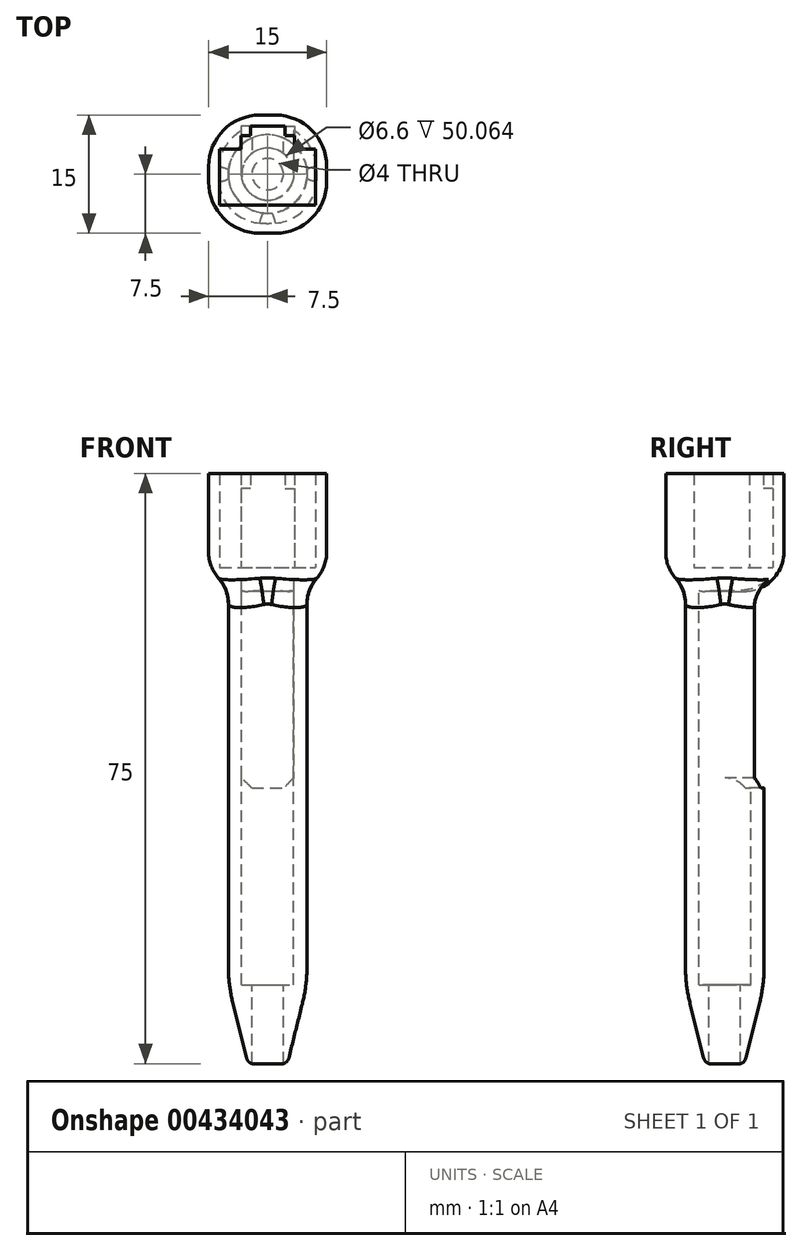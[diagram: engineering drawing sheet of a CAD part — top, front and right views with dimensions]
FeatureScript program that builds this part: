
annotation { "Feature Type Name" : "Feature", "Feature Type Description" : "" }
export const myFeature = defineFeature(function(context is Context, id is Id, definition is map)
    precondition{}
    {
        {
            var Q0;
            Q0=qCreatedBy(makeId("Top.planeOp"),FACE);
            var sketch = newSketch(context, id + "F0", { "sketchPlane" : qUnion([Q0])});
            skLineSegment(sketch, "E0.bottom", {"start": v(7.5, 7.5) * mm, "end": v(-7.5, 7.5) * mm});
            skLineSegment(sketch, "E0.top", {"start": v(7.5, -7.5) * mm, "end": v(-7.5, -7.5) * mm});
            skLineSegment(sketch, "E0.left", {"start": v(7.5, 7.5) * mm, "end": v(7.5, -7.5) * mm});
            skLineSegment(sketch, "E0.right", {"start": v(-7.5, 7.5) * mm, "end": v(-7.5, -7.5) * mm});
            skPoint(sketch, "E0.middle", {"position": v(0, 0) * mm});
            skLineSegment(sketch, "E1.bottom", {"start": v(-6.1, -3.94) * mm, "end": v(6.1, -3.94) * mm});
            skLineSegment(sketch, "E1.top", {"start": v(-6.1, 3.16) * mm, "end": v(6.1, 3.16) * mm});
            skLineSegment(sketch, "E1.left", {"start": v(-6.1, -3.94) * mm, "end": v(-6.1, 3.16) * mm});
            skLineSegment(sketch, "E1.right", {"start": v(6.1, -3.94) * mm, "end": v(6.1, 3.16) * mm});
            skLineSegment(sketch, "E2.bottom", {"start": v(-6.1, 3.16) * mm, "end": v(-3.4, 3.16) * mm, "construction": true});
            skLineSegment(sketch, "E2.top", {"start": v(-6.1, 3.16) * mm, "end": v(-3.4, 3.16) * mm, "construction": true});
            skLineSegment(sketch, "E2.left", {"start": v(-6.1, 3.16) * mm, "end": v(-6.1, 3.16) * mm});
            skLineSegment(sketch, "E2.right", {"start": v(-3.4, 3.16) * mm, "end": v(-3.4, 3.16) * mm});
            skLineSegment(sketch, "E3.bottom", {"start": v(6.1, 3.16) * mm, "end": v(3.4, 3.16) * mm, "construction": true});
            skLineSegment(sketch, "E3.top", {"start": v(6.1, 3.16) * mm, "end": v(3.4, 3.16) * mm, "construction": true});
            skLineSegment(sketch, "E3.left", {"start": v(6.1, 3.16) * mm, "end": v(6.1, 3.16) * mm});
            skLineSegment(sketch, "E3.right", {"start": v(3.4, 3.16) * mm, "end": v(3.4, 3.16) * mm});
            skLineSegment(sketch, "E4", {"start": v(-3.4, 3.16) * mm, "end": v(-3.4, 6.1) * mm});
            skLineSegment(sketch, "E5", {"start": v(-3.4, 6.1) * mm, "end": v(3.4, 6.1) * mm});
            skLineSegment(sketch, "E6", {"start": v(3.4, 3.16) * mm, "end": v(3.4, 6.1) * mm});
            skLineSegment(sketch, "E7", {"start": v(-6.1, -3.94) * mm, "end": v(-6.1, 1.06) * mm, "construction": true});
            skLineSegment(sketch, "E8", {"start": v(-7.5, 7.5) * mm, "end": v(0, 7.5) * mm, "construction": true});
            skLineSegment(sketch, "E9", {"start": v(0, 7.5) * mm, "end": v(0, -7.5) * mm, "construction": true});
            skLineSegment(sketch, "E10", {"start": v(0, 3.16) * mm, "end": v(0, -3.94) * mm, "construction": true});
            skSolve(sketch);
        }
        {
            var Q0;
            Q0=makeQuery(id+"F0.imprint","IMPRINT",FACE,{"disambiguationData":[TD([[makeQuery(id+"F0.imprint","IMPRINT",EDGE,{"derivedFrom":sQuery(id+"F0.wireOp",EDGE,"E0.bottom")}),1.0]])]});
            extrude(context, id + "F1", {"entities" : qUnion([Q0]), "depth" : 12 * mm});
        }
        {
            var Q0;
            Q0=makeQuery(id+"F1.opExtrude","SWEPT_FACE",FACE,{"disambiguationData":[OSD([sQuery(id+"F0.wireOp",EDGE,"E6")])]});
            var sketch = newSketch(context, id + "F2", { "sketchPlane" : qUnion([Q0])});
            skLineSegment(sketch, "E11.bottom", {"start": v(-6.1, 12) * mm, "end": v(-4.9, 12) * mm});
            skLineSegment(sketch, "E11.top", {"start": v(-6.1, 10.05) * mm, "end": v(-4.9, 10.05) * mm});
            skLineSegment(sketch, "E11.left", {"start": v(-6.1, 12) * mm, "end": v(-6.1, 10.05) * mm});
            skLineSegment(sketch, "E11.right", {"start": v(-4.9, 12) * mm, "end": v(-4.9, 10.05) * mm});
            skSolve(sketch);
        }
        {
            var Q0;
            Q0 = qSketchRegion(id + "F2", true);
            extrude(context, id + "F3", {"entities" : qUnion([Q0]), "operationType" : NewBodyOperationType.ADD, "depth" : 1.21 * mm});
        }
        {
            var Q0;
            Q0=makeQuery(id+"F1.opExtrude","SWEPT_FACE",FACE,{"disambiguationData":[OSD([sQuery(id+"F0.wireOp",EDGE,"E4")])]});
            var sketch = newSketch(context, id + "F4", { "sketchPlane" : qUnion([Q0])});
            skLineSegment(sketch, "E12.bottom", {"start": v(6.1, 12) * mm, "end": v(4.9, 12) * mm});
            skLineSegment(sketch, "E12.top", {"start": v(6.1, 10.05) * mm, "end": v(4.9, 10.05) * mm});
            skLineSegment(sketch, "E12.left", {"start": v(6.1, 12) * mm, "end": v(6.1, 10.05) * mm});
            skLineSegment(sketch, "E12.right", {"start": v(4.9, 12) * mm, "end": v(4.9, 10.05) * mm});
            skSolve(sketch);
        }
        {
            var Q0;
            Q0=makeQuery(id+"F4.imprint","IMPRINT",FACE,{"disambiguationData":[TD([[makeQuery(id+"F4.imprint","IMPRINT",EDGE,{"derivedFrom":sQuery(id+"F4.wireOp",EDGE,"E12.bottom")}),-1.0]])]});
            extrude(context, id + "F5", {"entities" : qUnion([Q0]), "operationType" : NewBodyOperationType.ADD, "depth" : 1.21 * mm});
        }
        {
            var Q0;
            Q0=makeQuery(id+"F1.opExtrude","CAP_FACE",FACE,{"disambiguationData":[OSD([sQuery(id+"F0.wireOp",EDGE,"E0.bottom"),sQuery(id+"F0.wireOp",EDGE,"E0.top"),sQuery(id+"F0.wireOp",EDGE,"E0.left"),sQuery(id+"F0.wireOp",EDGE,"E0.right"),sQuery(id+"F0.wireOp",EDGE,"E1.bottom"),sQuery(id+"F0.wireOp",EDGE,"E1.top"),sQuery(id+"F0.wireOp",EDGE,"E1.left"),sQuery(id+"F0.wireOp",EDGE,"E1.right"),sQuery(id+"F0.wireOp",EDGE,"E4"),sQuery(id+"F0.wireOp",EDGE,"E5"),sQuery(id+"F0.wireOp",EDGE,"E6")])],"isStart":true});
            var sketch = newSketch(context, id + "F6", { "sketchPlane" : qUnion([Q0])});
            skLineSegment(sketch, "E13.bottom", {"start": v(-7.5, 7.5) * mm, "end": v(7.5, 7.5) * mm});
            skLineSegment(sketch, "E13.top", {"start": v(-7.5, -7.5) * mm, "end": v(7.5, -7.5) * mm});
            skLineSegment(sketch, "E13.left", {"start": v(-7.5, 7.5) * mm, "end": v(-7.5, -7.5) * mm});
            skLineSegment(sketch, "E13.right", {"start": v(7.5, 7.5) * mm, "end": v(7.5, -7.5) * mm});
            skSolve(sketch);
        }
        {
            var Q0;
            Q0 = qSketchRegion(id + "F6", true);
            extrude(context, id + "F7", {"entities" : qUnion([Q0]), "operationType" : NewBodyOperationType.ADD, "depth" : 3 * mm});
        }
        {
            var Q0;
            Q0=makeQuery(id+"F7.opExtrude","CAP_FACE",FACE,{"disambiguationData":[OSD([sQuery(id+"F6.wireOp",EDGE,"E13.bottom"),sQuery(id+"F6.wireOp",EDGE,"E13.top"),sQuery(id+"F6.wireOp",EDGE,"E13.left"),sQuery(id+"F6.wireOp",EDGE,"E13.right")])],"isStart":false});
            var sketch = newSketch(context, id + "F8", { "sketchPlane" : qUnion([Q0])});
            skCircle(sketch, "E14", {"center": v(0, 0) * mm, "radius": 3.3 * mm});
            skCircle(sketch, "E15", {"center": v(0, 0) * mm, "radius": 5 * mm});
            skSolve(sketch);
        }
        {
            var Q0;
            Q0=makeQuery(id+"F8.imprint","IMPRINT",FACE,{"disambiguationData":[TD([[makeQuery(id+"F8.imprint","IMPRINT",EDGE,{"derivedFrom":sQuery(id+"F8.wireOp",EDGE,"E14")}),-1.0]])]});
            extrude(context, id + "F9", {"entities" : qUnion([Q0]), "operationType" : NewBodyOperationType.ADD, "depth" : 50 * mm});
        }
        {
            var Q0;
            Q0=makeQuery(id+"F7.boolean.opBoolean","MERGE",FACE,{"derivedFrom":[makeQuery(id+"F1.opExtrude","SWEPT_FACE",FACE,{"disambiguationData":[OSD([sQuery(id+"F0.wireOp",EDGE,"E0.bottom")])]}),makeQuery(id+"F7.opExtrude","SWEPT_FACE",FACE,{"disambiguationData":[OSD([sQuery(id+"F6.wireOp",EDGE,"E13.top")])]})]});
            var sketch = newSketch(context, id + "F10", { "sketchPlane" : qUnion([Q0])});
            skLineSegment(sketch, "E16", {"start": v(-3.3, -3) * mm, "end": v(3.3, -3) * mm, "construction": true});
            skPoint(sketch, "E17", {"position": v(0, -3) * mm});
            skLineSegment(sketch, "E18", {"start": v(-3.3, -3) * mm, "end": v(-3.3, -28) * mm});
            skLineSegment(sketch, "E19", {"start": v(-3.3, -28) * mm, "end": v(3.3, -28) * mm});
            skLineSegment(sketch, "E20", {"start": v(3.3, -28) * mm, "end": v(3.3, -3) * mm});
            skPoint(sketch, "E21", {"position": v(0, -28) * mm});
            skLineSegment(sketch, "E22.bottom", {"start": v(-2, -28) * mm, "end": v(2, -28) * mm});
            skLineSegment(sketch, "E22.top", {"start": v(-2, -73) * mm, "end": v(2, -73) * mm});
            skLineSegment(sketch, "E22.left", {"start": v(-2, -28) * mm, "end": v(-2, -73) * mm});
            skLineSegment(sketch, "E22.right", {"start": v(2, -28) * mm, "end": v(2, -73) * mm});
            skSolve(sketch);
        }
        {
            var Q0;
            Q0=makeQuery(id+"F9.opExtrude","CAP_FACE",FACE,{"disambiguationData":[OSD([sQuery(id+"F8.wireOp",EDGE,"E14"),sQuery(id+"F8.wireOp",EDGE,"E15")])],"isStart":false});
            var sketch = newSketch(context, id + "F11", { "sketchPlane" : qUnion([Q0])});
            skCircle(sketch, "E23", {"center": v(0, 0) * mm, "radius": 5 * mm});
            skCircle(sketch, "E24", {"center": v(0, 0) * mm, "radius": 2 * mm});
            skSolve(sketch);
        }
        {
            var Q0;
            Q0=makeQuery(id+"F11.imprint","IMPRINT",FACE,{"disambiguationData":[TD([[makeQuery(id+"F11.imprint","IMPRINT",EDGE,{"derivedFrom":makeQuery(id+"F9.opExtrude","CAP_EDGE",EDGE,{"disambiguationData":[OSD([sQuery(id+"F8.wireOp",EDGE,"E14")])],"isStart":false})}),-1.0]])]});
            var Q1;
            Q1=makeQuery(id+"F11.imprint","IMPRINT",FACE,{"disambiguationData":[TD([[makeQuery(id+"F11.imprint","IMPRINT",EDGE,{"derivedFrom":sQuery(id+"F11.wireOp",EDGE,"E24")}),-1.0]])]});
            extrude(context, id + "F12", {"entities" : qUnion([Q0, Q1]), "operationType" : NewBodyOperationType.ADD, "depth" : 10 * mm});
        }
        {
            var Q0;
            Q0=makeQuery(id+"F10.imprint","IMPRINT",FACE,{"disambiguationData":[TD([[makeQuery(id+"F10.imprint","IMPRINT",EDGE,{"derivedFrom":sQuery(id+"F10.wireOp",EDGE,"E22.bottom")}),-1.0]])]});
            var Q1;
            {var subQ3=sQuery(id+"F10.wireOp",EDGE,"E18");Q1=makeQuery(id+"F10.imprint","IMPRINT",FACE,{"disambiguationData":[TD([[makeQuery(id+"F10.imprint","IMPRINT",EDGE,{"derivedFrom":subQ3}),1.0]])]});}
            extrude(context, id + "F13", {"entities" : qUnion([Q0, Q1]), "operationType" : NewBodyOperationType.REMOVE, "oppositeDirection" : true, "depth" : 7.5 * mm});
        }
        {
            var Q0;
            Q0=makeQuery(id+"F12.opExtrude","CAP_EDGE",EDGE,{"disambiguationData":[OSD([sQuery(id+"F11.wireOp",EDGE,"E23")])],"isStart":false});
            chamfer(context, id + "F14", {"entities" : qUnion([Q0]), "chamferType" : ChamferType.TWO_OFFSETS, "width1" : 2.5 * mm, "oppositeDirection" : false, "width2" : 10 * mm, "tangentPropagation" : true});
        }
        {
            var Q0;
            {var subQ0=sQuery(id+"F11.wireOp",EDGE,"E23");Q0=makeQuery(id+"F14.opChamfer","BLEND_EDGE",EDGE,{"blendedFrom":[makeQuery(id+"F12.opExtrude","CAP_EDGE",EDGE,{"disambiguationData":[OSD([subQ0])],"isStart":false}),makeQuery(id+"F12.boolean.opBoolean","MERGE",FACE,{"derivedFrom":[makeQuery(id+"F9.opExtrude","SWEPT_FACE",FACE,{"disambiguationData":[OSD([sQuery(id+"F8.wireOp",EDGE,"E15")])]}),makeQuery(id+"F12.opExtrude","SWEPT_FACE",FACE,{"disambiguationData":[OSD([subQ0])]})]})],"blendedInto":[makeQuery(id+"F12.boolean.opBoolean","MERGE",FACE,{"derivedFrom":[makeQuery(id+"F9.opExtrude","SWEPT_FACE",FACE,{"disambiguationData":[OSD([sQuery(id+"F8.wireOp",EDGE,"E15")])]}),makeQuery(id+"F12.opExtrude","SWEPT_FACE",FACE,{"disambiguationData":[OSD([subQ0])]})]})]});}
            fillet(context, id + "F15", {"entities" : qUnion([Q0]), "radius" : 20 * mm, "tangentPropagation" : true, "allowEdgeOverflow" : false});
        }
        {
            var Q0;
            {var subQ0=sQuery(id+"F11.wireOp",EDGE,"E23");Q0=makeQuery(id+"F14.opChamfer","BLEND_EDGE",EDGE,{"blendedFrom":[makeQuery(id+"F12.opExtrude","CAP_EDGE",EDGE,{"disambiguationData":[OSD([subQ0])],"isStart":false}),makeQuery(id+"F12.opExtrude","CAP_FACE",FACE,{"disambiguationData":[OSD([subQ0,sQuery(id+"F11.wireOp",EDGE,"E24")])],"isStart":false})],"blendedInto":[makeQuery(id+"F12.opExtrude","CAP_FACE",FACE,{"disambiguationData":[OSD([subQ0,sQuery(id+"F11.wireOp",EDGE,"E24")])],"isStart":false})]});}
            fillet(context, id + "F16", {"entities" : qUnion([Q0]), "radius" : 1 * mm, "tangentPropagation" : true, "allowEdgeOverflow" : false});
        }
        {
            var Q0;
            Q0=makeQuery(id+"F7.boolean.opBoolean","MERGE",EDGE,{"derivedFrom":[makeQuery(id+"F1.opExtrude","SWEPT_EDGE",EDGE,{"disambiguationData":[OSD([sQuery(id+"F0.wireOp",EDGE,"E0.bottom"),sQuery(id+"F0.wireOp",EDGE,"E0.right")])]}),makeQuery(id+"F7.opExtrude","SWEPT_EDGE",EDGE,{"disambiguationData":[OSD([sQuery(id+"F6.wireOp",EDGE,"E13.top"),sQuery(id+"F6.wireOp",EDGE,"E13.left")])]})]});
            var Q1;
            Q1=makeQuery(id+"F7.boolean.opBoolean","MERGE",EDGE,{"derivedFrom":[makeQuery(id+"F1.opExtrude","SWEPT_EDGE",EDGE,{"disambiguationData":[OSD([sQuery(id+"F0.wireOp",EDGE,"E0.top"),sQuery(id+"F0.wireOp",EDGE,"E0.right")])]}),makeQuery(id+"F7.opExtrude","SWEPT_EDGE",EDGE,{"disambiguationData":[OSD([sQuery(id+"F6.wireOp",EDGE,"E13.bottom"),sQuery(id+"F6.wireOp",EDGE,"E13.left")])]})]});
            var Q2;
            Q2=makeQuery(id+"F7.boolean.opBoolean","MERGE",EDGE,{"derivedFrom":[makeQuery(id+"F1.opExtrude","SWEPT_EDGE",EDGE,{"disambiguationData":[OSD([sQuery(id+"F0.wireOp",EDGE,"E0.bottom"),sQuery(id+"F0.wireOp",EDGE,"E0.left")])]}),makeQuery(id+"F7.opExtrude","SWEPT_EDGE",EDGE,{"disambiguationData":[OSD([sQuery(id+"F6.wireOp",EDGE,"E13.top"),sQuery(id+"F6.wireOp",EDGE,"E13.right")])]})]});
            var Q3;
            Q3=makeQuery(id+"F7.boolean.opBoolean","MERGE",EDGE,{"derivedFrom":[makeQuery(id+"F1.opExtrude","SWEPT_EDGE",EDGE,{"disambiguationData":[OSD([sQuery(id+"F0.wireOp",EDGE,"E0.top"),sQuery(id+"F0.wireOp",EDGE,"E0.left")])]}),makeQuery(id+"F7.opExtrude","SWEPT_EDGE",EDGE,{"disambiguationData":[OSD([sQuery(id+"F6.wireOp",EDGE,"E13.bottom"),sQuery(id+"F6.wireOp",EDGE,"E13.right")])]})]});
            fillet(context, id + "F17", {"entities" : qUnion([Q0, Q1, Q2, Q3]), "radius" : 6.5 * mm, "tangentPropagation" : true, "allowEdgeOverflow" : false});
        }
        {
            var Q0;
            {var subQ0=sQuery(id+"F6.wireOp",EDGE,"E13.top");var subQ1=sQuery(id+"F6.wireOp",EDGE,"E13.right");var subQ2=sQuery(id+"F6.wireOp",EDGE,"E13.left");var subQ3=sQuery(id+"F6.wireOp",EDGE,"E13.bottom");var subQ4=makeQuery(id+"F7.opExtrude","CAP_FACE",FACE,{"disambiguationData":[OSD([subQ3,subQ0,subQ2,subQ1])],"isStart":false});var subQ5=sQuery(id+"F0.wireOp",EDGE,"E0.top");var subQ6=sQuery(id+"F0.wireOp",EDGE,"E0.right");Q0=makeQuery(id+"F17.opFillet","BLEND_EDGE",EDGE,{"blendedFrom":[makeQuery(id+"F7.boolean.opBoolean","MERGE",EDGE,{"derivedFrom":[makeQuery(id+"F1.opExtrude","SWEPT_EDGE",EDGE,{"disambiguationData":[OSD([subQ5,subQ6])]}),makeQuery(id+"F7.opExtrude","SWEPT_EDGE",EDGE,{"disambiguationData":[OSD([subQ3,subQ2])]})]}),makeQuery(id+"F13.boolean.opBoolean","MERGE",FACE,{"derivedFrom":[makeQuery(id+"F9.boolean.opBoolean","SPLIT",FACE,{"disambiguationData":[TD([makeQuery(id+"F1.opExtrude","SWEPT_FACE",FACE,{"disambiguationData":[OSD([sQuery(id+"F0.wireOp",EDGE,"E0.bottom")])]})])],"derivedFrom":subQ4}),makeQuery(id+"F9.boolean.opBoolean","SPLIT",FACE,{"disambiguationData":[TD([makeQuery(id+"F9.opExtrude","SWEPT_FACE",FACE,{"disambiguationData":[OSD([sQuery(id+"F8.wireOp",EDGE,"E14")])]})])],"derivedFrom":subQ4}),makeQuery(id+"F13.opExtrude","SWEPT_FACE",FACE,{"disambiguationData":[OSD([subQ0])]})]})],"blendedInto":[makeQuery(id+"F13.boolean.opBoolean","MERGE",FACE,{"derivedFrom":[makeQuery(id+"F9.boolean.opBoolean","SPLIT",FACE,{"disambiguationData":[TD([makeQuery(id+"F1.opExtrude","SWEPT_FACE",FACE,{"disambiguationData":[OSD([sQuery(id+"F0.wireOp",EDGE,"E0.bottom")])]})])],"derivedFrom":subQ4}),makeQuery(id+"F9.boolean.opBoolean","SPLIT",FACE,{"disambiguationData":[TD([makeQuery(id+"F9.opExtrude","SWEPT_FACE",FACE,{"disambiguationData":[OSD([sQuery(id+"F8.wireOp",EDGE,"E14")])]})])],"derivedFrom":subQ4}),makeQuery(id+"F13.opExtrude","SWEPT_FACE",FACE,{"disambiguationData":[OSD([subQ0])]})]})]});}
            var Q1;
            Q1=makeQuery(id+"F7.opExtrude","CAP_EDGE",EDGE,{"disambiguationData":[OSD([sQuery(id+"F6.wireOp",EDGE,"E13.bottom")])],"isStart":false});
            var Q2;
            {var subQ0=sQuery(id+"F6.wireOp",EDGE,"E13.top");var subQ1=sQuery(id+"F6.wireOp",EDGE,"E13.right");var subQ2=sQuery(id+"F6.wireOp",EDGE,"E13.left");var subQ3=sQuery(id+"F6.wireOp",EDGE,"E13.bottom");var subQ4=makeQuery(id+"F7.opExtrude","CAP_FACE",FACE,{"disambiguationData":[OSD([subQ3,subQ0,subQ2,subQ1])],"isStart":false});var subQ5=sQuery(id+"F0.wireOp",EDGE,"E0.left");var subQ6=sQuery(id+"F0.wireOp",EDGE,"E0.top");Q2=makeQuery(id+"F17.opFillet","BLEND_EDGE",EDGE,{"blendedFrom":[makeQuery(id+"F7.boolean.opBoolean","MERGE",EDGE,{"derivedFrom":[makeQuery(id+"F1.opExtrude","SWEPT_EDGE",EDGE,{"disambiguationData":[OSD([subQ6,subQ5])]}),makeQuery(id+"F7.opExtrude","SWEPT_EDGE",EDGE,{"disambiguationData":[OSD([subQ3,subQ1])]})]}),makeQuery(id+"F13.boolean.opBoolean","MERGE",FACE,{"derivedFrom":[makeQuery(id+"F9.boolean.opBoolean","SPLIT",FACE,{"disambiguationData":[TD([makeQuery(id+"F1.opExtrude","SWEPT_FACE",FACE,{"disambiguationData":[OSD([sQuery(id+"F0.wireOp",EDGE,"E0.bottom")])]})])],"derivedFrom":subQ4}),makeQuery(id+"F9.boolean.opBoolean","SPLIT",FACE,{"disambiguationData":[TD([makeQuery(id+"F9.opExtrude","SWEPT_FACE",FACE,{"disambiguationData":[OSD([sQuery(id+"F8.wireOp",EDGE,"E14")])]})])],"derivedFrom":subQ4}),makeQuery(id+"F13.opExtrude","SWEPT_FACE",FACE,{"disambiguationData":[OSD([subQ0])]})]})],"blendedInto":[makeQuery(id+"F13.boolean.opBoolean","MERGE",FACE,{"derivedFrom":[makeQuery(id+"F9.boolean.opBoolean","SPLIT",FACE,{"disambiguationData":[TD([makeQuery(id+"F1.opExtrude","SWEPT_FACE",FACE,{"disambiguationData":[OSD([sQuery(id+"F0.wireOp",EDGE,"E0.bottom")])]})])],"derivedFrom":subQ4}),makeQuery(id+"F9.boolean.opBoolean","SPLIT",FACE,{"disambiguationData":[TD([makeQuery(id+"F9.opExtrude","SWEPT_FACE",FACE,{"disambiguationData":[OSD([sQuery(id+"F8.wireOp",EDGE,"E14")])]})])],"derivedFrom":subQ4}),makeQuery(id+"F13.opExtrude","SWEPT_FACE",FACE,{"disambiguationData":[OSD([subQ0])]})]})]});}
            fillet(context, id + "F18", {"entities" : qUnion([Q0, Q1, Q2]), "radius" : 5 * mm, "tangentPropagation" : true, "allowEdgeOverflow" : false});
        }
        {
            var Q0;
            {var subQ0=makeQuery(id+"F9.opExtrude","SWEPT_FACE",FACE,{"disambiguationData":[OSD([sQuery(id+"F8.wireOp",EDGE,"E15")])]});var subQ1=sQuery(id+"F6.wireOp",EDGE,"E13.top");var subQ2=sQuery(id+"F6.wireOp",EDGE,"E13.right");var subQ3=sQuery(id+"F6.wireOp",EDGE,"E13.left");var subQ4=sQuery(id+"F6.wireOp",EDGE,"E13.bottom");var subQ5=makeQuery(id+"F7.opExtrude","CAP_FACE",FACE,{"disambiguationData":[OSD([subQ4,subQ1,subQ3,subQ2])],"isStart":false});var subQ6=sQuery(id+"F0.wireOp",EDGE,"E0.right");var subQ7=sQuery(id+"F0.wireOp",EDGE,"E0.bottom");Q0=makeQuery(id+"F18.opFillet","BLEND_EDGE",EDGE,{"blendedFrom":[makeQuery(id+"F17.opFillet","BLEND_EDGE",EDGE,{"blendedFrom":[makeQuery(id+"F7.boolean.opBoolean","MERGE",EDGE,{"derivedFrom":[makeQuery(id+"F1.opExtrude","SWEPT_EDGE",EDGE,{"disambiguationData":[OSD([subQ7,subQ6])]}),makeQuery(id+"F7.opExtrude","SWEPT_EDGE",EDGE,{"disambiguationData":[OSD([subQ1,subQ3])]})]}),makeQuery(id+"F13.boolean.opBoolean","MERGE",FACE,{"derivedFrom":[makeQuery(id+"F9.boolean.opBoolean","SPLIT",FACE,{"disambiguationData":[TD([makeQuery(id+"F1.opExtrude","SWEPT_FACE",FACE,{"disambiguationData":[OSD([subQ7])]})])],"derivedFrom":subQ5}),makeQuery(id+"F9.boolean.opBoolean","SPLIT",FACE,{"disambiguationData":[TD([makeQuery(id+"F9.opExtrude","SWEPT_FACE",FACE,{"disambiguationData":[OSD([sQuery(id+"F8.wireOp",EDGE,"E14")])]})])],"derivedFrom":subQ5}),makeQuery(id+"F13.opExtrude","SWEPT_FACE",FACE,{"disambiguationData":[OSD([subQ1])]})]})],"blendedInto":[makeQuery(id+"F13.boolean.opBoolean","MERGE",FACE,{"derivedFrom":[makeQuery(id+"F9.boolean.opBoolean","SPLIT",FACE,{"disambiguationData":[TD([makeQuery(id+"F1.opExtrude","SWEPT_FACE",FACE,{"disambiguationData":[OSD([subQ7])]})])],"derivedFrom":subQ5}),makeQuery(id+"F9.boolean.opBoolean","SPLIT",FACE,{"disambiguationData":[TD([makeQuery(id+"F9.opExtrude","SWEPT_FACE",FACE,{"disambiguationData":[OSD([sQuery(id+"F8.wireOp",EDGE,"E14")])]})])],"derivedFrom":subQ5}),makeQuery(id+"F13.opExtrude","SWEPT_FACE",FACE,{"disambiguationData":[OSD([subQ1])]})]})]}),makeQuery(id+"F12.boolean.opBoolean","MERGE",FACE,{"derivedFrom":[subQ0,makeQuery(id+"F12.opExtrude","SWEPT_FACE",FACE,{"disambiguationData":[OSD([sQuery(id+"F11.wireOp",EDGE,"E23")])]})]})],"blendedInto":[makeQuery(id+"F12.boolean.opBoolean","MERGE",FACE,{"derivedFrom":[subQ0,makeQuery(id+"F12.opExtrude","SWEPT_FACE",FACE,{"disambiguationData":[OSD([sQuery(id+"F11.wireOp",EDGE,"E23")])]})]})]});}
            var Q1;
            Q1=makeQuery(id+"F18.opFillet","BLEND_EDGE",EDGE,{"blendedFrom":[makeQuery(id+"F7.opExtrude","CAP_EDGE",EDGE,{"disambiguationData":[OSD([sQuery(id+"F6.wireOp",EDGE,"E13.left")])],"isStart":false}),makeQuery(id+"F12.boolean.opBoolean","MERGE",FACE,{"derivedFrom":[makeQuery(id+"F9.opExtrude","SWEPT_FACE",FACE,{"disambiguationData":[OSD([sQuery(id+"F8.wireOp",EDGE,"E15")])]}),makeQuery(id+"F12.opExtrude","SWEPT_FACE",FACE,{"disambiguationData":[OSD([sQuery(id+"F11.wireOp",EDGE,"E23")])]})]})],"blendedInto":[makeQuery(id+"F12.boolean.opBoolean","MERGE",FACE,{"derivedFrom":[makeQuery(id+"F9.opExtrude","SWEPT_FACE",FACE,{"disambiguationData":[OSD([sQuery(id+"F8.wireOp",EDGE,"E15")])]}),makeQuery(id+"F12.opExtrude","SWEPT_FACE",FACE,{"disambiguationData":[OSD([sQuery(id+"F11.wireOp",EDGE,"E23")])]})]})]});
            var Q2;
            {var subQ0=makeQuery(id+"F9.opExtrude","SWEPT_FACE",FACE,{"disambiguationData":[OSD([sQuery(id+"F8.wireOp",EDGE,"E15")])]});var subQ1=sQuery(id+"F6.wireOp",EDGE,"E13.top");var subQ2=sQuery(id+"F6.wireOp",EDGE,"E13.right");var subQ3=sQuery(id+"F6.wireOp",EDGE,"E13.left");var subQ4=sQuery(id+"F6.wireOp",EDGE,"E13.bottom");var subQ5=makeQuery(id+"F7.opExtrude","CAP_FACE",FACE,{"disambiguationData":[OSD([subQ4,subQ1,subQ3,subQ2])],"isStart":false});var subQ6=sQuery(id+"F0.wireOp",EDGE,"E0.top");var subQ7=sQuery(id+"F0.wireOp",EDGE,"E0.right");Q2=makeQuery(id+"F18.opFillet","BLEND_EDGE",EDGE,{"blendedFrom":[makeQuery(id+"F17.opFillet","BLEND_EDGE",EDGE,{"blendedFrom":[makeQuery(id+"F7.boolean.opBoolean","MERGE",EDGE,{"derivedFrom":[makeQuery(id+"F1.opExtrude","SWEPT_EDGE",EDGE,{"disambiguationData":[OSD([subQ6,subQ7])]}),makeQuery(id+"F7.opExtrude","SWEPT_EDGE",EDGE,{"disambiguationData":[OSD([subQ4,subQ3])]})]}),makeQuery(id+"F13.boolean.opBoolean","MERGE",FACE,{"derivedFrom":[makeQuery(id+"F9.boolean.opBoolean","SPLIT",FACE,{"disambiguationData":[TD([makeQuery(id+"F1.opExtrude","SWEPT_FACE",FACE,{"disambiguationData":[OSD([sQuery(id+"F0.wireOp",EDGE,"E0.bottom")])]})])],"derivedFrom":subQ5}),makeQuery(id+"F9.boolean.opBoolean","SPLIT",FACE,{"disambiguationData":[TD([makeQuery(id+"F9.opExtrude","SWEPT_FACE",FACE,{"disambiguationData":[OSD([sQuery(id+"F8.wireOp",EDGE,"E14")])]})])],"derivedFrom":subQ5}),makeQuery(id+"F13.opExtrude","SWEPT_FACE",FACE,{"disambiguationData":[OSD([subQ1])]})]})],"blendedInto":[makeQuery(id+"F13.boolean.opBoolean","MERGE",FACE,{"derivedFrom":[makeQuery(id+"F9.boolean.opBoolean","SPLIT",FACE,{"disambiguationData":[TD([makeQuery(id+"F1.opExtrude","SWEPT_FACE",FACE,{"disambiguationData":[OSD([sQuery(id+"F0.wireOp",EDGE,"E0.bottom")])]})])],"derivedFrom":subQ5}),makeQuery(id+"F9.boolean.opBoolean","SPLIT",FACE,{"disambiguationData":[TD([makeQuery(id+"F9.opExtrude","SWEPT_FACE",FACE,{"disambiguationData":[OSD([sQuery(id+"F8.wireOp",EDGE,"E14")])]})])],"derivedFrom":subQ5}),makeQuery(id+"F13.opExtrude","SWEPT_FACE",FACE,{"disambiguationData":[OSD([subQ1])]})]})]}),makeQuery(id+"F12.boolean.opBoolean","MERGE",FACE,{"derivedFrom":[subQ0,makeQuery(id+"F12.opExtrude","SWEPT_FACE",FACE,{"disambiguationData":[OSD([sQuery(id+"F11.wireOp",EDGE,"E23")])]})]})],"blendedInto":[makeQuery(id+"F12.boolean.opBoolean","MERGE",FACE,{"derivedFrom":[subQ0,makeQuery(id+"F12.opExtrude","SWEPT_FACE",FACE,{"disambiguationData":[OSD([sQuery(id+"F11.wireOp",EDGE,"E23")])]})]})]});}
            var Q3;
            Q3=makeQuery(id+"F18.opFillet","BLEND_EDGE",EDGE,{"blendedFrom":[makeQuery(id+"F7.opExtrude","CAP_EDGE",EDGE,{"disambiguationData":[OSD([sQuery(id+"F6.wireOp",EDGE,"E13.bottom")])],"isStart":false}),makeQuery(id+"F12.boolean.opBoolean","MERGE",FACE,{"derivedFrom":[makeQuery(id+"F9.opExtrude","SWEPT_FACE",FACE,{"disambiguationData":[OSD([sQuery(id+"F8.wireOp",EDGE,"E15")])]}),makeQuery(id+"F12.opExtrude","SWEPT_FACE",FACE,{"disambiguationData":[OSD([sQuery(id+"F11.wireOp",EDGE,"E23")])]})]})],"blendedInto":[makeQuery(id+"F12.boolean.opBoolean","MERGE",FACE,{"derivedFrom":[makeQuery(id+"F9.opExtrude","SWEPT_FACE",FACE,{"disambiguationData":[OSD([sQuery(id+"F8.wireOp",EDGE,"E15")])]}),makeQuery(id+"F12.opExtrude","SWEPT_FACE",FACE,{"disambiguationData":[OSD([sQuery(id+"F11.wireOp",EDGE,"E23")])]})]})]});
            var Q4;
            {var subQ0=makeQuery(id+"F9.opExtrude","SWEPT_FACE",FACE,{"disambiguationData":[OSD([sQuery(id+"F8.wireOp",EDGE,"E15")])]});var subQ1=sQuery(id+"F6.wireOp",EDGE,"E13.top");var subQ2=sQuery(id+"F6.wireOp",EDGE,"E13.right");var subQ3=sQuery(id+"F6.wireOp",EDGE,"E13.left");var subQ4=sQuery(id+"F6.wireOp",EDGE,"E13.bottom");var subQ5=makeQuery(id+"F7.opExtrude","CAP_FACE",FACE,{"disambiguationData":[OSD([subQ4,subQ1,subQ3,subQ2])],"isStart":false});var subQ6=sQuery(id+"F0.wireOp",EDGE,"E0.left");var subQ7=sQuery(id+"F0.wireOp",EDGE,"E0.top");Q4=makeQuery(id+"F18.opFillet","BLEND_EDGE",EDGE,{"blendedFrom":[makeQuery(id+"F17.opFillet","BLEND_EDGE",EDGE,{"blendedFrom":[makeQuery(id+"F7.boolean.opBoolean","MERGE",EDGE,{"derivedFrom":[makeQuery(id+"F1.opExtrude","SWEPT_EDGE",EDGE,{"disambiguationData":[OSD([subQ7,subQ6])]}),makeQuery(id+"F7.opExtrude","SWEPT_EDGE",EDGE,{"disambiguationData":[OSD([subQ4,subQ2])]})]}),makeQuery(id+"F13.boolean.opBoolean","MERGE",FACE,{"derivedFrom":[makeQuery(id+"F9.boolean.opBoolean","SPLIT",FACE,{"disambiguationData":[TD([makeQuery(id+"F1.opExtrude","SWEPT_FACE",FACE,{"disambiguationData":[OSD([sQuery(id+"F0.wireOp",EDGE,"E0.bottom")])]})])],"derivedFrom":subQ5}),makeQuery(id+"F9.boolean.opBoolean","SPLIT",FACE,{"disambiguationData":[TD([makeQuery(id+"F9.opExtrude","SWEPT_FACE",FACE,{"disambiguationData":[OSD([sQuery(id+"F8.wireOp",EDGE,"E14")])]})])],"derivedFrom":subQ5}),makeQuery(id+"F13.opExtrude","SWEPT_FACE",FACE,{"disambiguationData":[OSD([subQ1])]})]})],"blendedInto":[makeQuery(id+"F13.boolean.opBoolean","MERGE",FACE,{"derivedFrom":[makeQuery(id+"F9.boolean.opBoolean","SPLIT",FACE,{"disambiguationData":[TD([makeQuery(id+"F1.opExtrude","SWEPT_FACE",FACE,{"disambiguationData":[OSD([sQuery(id+"F0.wireOp",EDGE,"E0.bottom")])]})])],"derivedFrom":subQ5}),makeQuery(id+"F9.boolean.opBoolean","SPLIT",FACE,{"disambiguationData":[TD([makeQuery(id+"F9.opExtrude","SWEPT_FACE",FACE,{"disambiguationData":[OSD([sQuery(id+"F8.wireOp",EDGE,"E14")])]})])],"derivedFrom":subQ5}),makeQuery(id+"F13.opExtrude","SWEPT_FACE",FACE,{"disambiguationData":[OSD([subQ1])]})]})]}),makeQuery(id+"F12.boolean.opBoolean","MERGE",FACE,{"derivedFrom":[subQ0,makeQuery(id+"F12.opExtrude","SWEPT_FACE",FACE,{"disambiguationData":[OSD([sQuery(id+"F11.wireOp",EDGE,"E23")])]})]})],"blendedInto":[makeQuery(id+"F12.boolean.opBoolean","MERGE",FACE,{"derivedFrom":[subQ0,makeQuery(id+"F12.opExtrude","SWEPT_FACE",FACE,{"disambiguationData":[OSD([sQuery(id+"F11.wireOp",EDGE,"E23")])]})]})]});}
            var Q5;
            Q5=makeQuery(id+"F18.opFillet","BLEND_EDGE",EDGE,{"blendedFrom":[makeQuery(id+"F7.opExtrude","CAP_EDGE",EDGE,{"disambiguationData":[OSD([sQuery(id+"F6.wireOp",EDGE,"E13.right")])],"isStart":false}),makeQuery(id+"F12.boolean.opBoolean","MERGE",FACE,{"derivedFrom":[makeQuery(id+"F9.opExtrude","SWEPT_FACE",FACE,{"disambiguationData":[OSD([sQuery(id+"F8.wireOp",EDGE,"E15")])]}),makeQuery(id+"F12.opExtrude","SWEPT_FACE",FACE,{"disambiguationData":[OSD([sQuery(id+"F11.wireOp",EDGE,"E23")])]})]})],"blendedInto":[makeQuery(id+"F12.boolean.opBoolean","MERGE",FACE,{"derivedFrom":[makeQuery(id+"F9.opExtrude","SWEPT_FACE",FACE,{"disambiguationData":[OSD([sQuery(id+"F8.wireOp",EDGE,"E15")])]}),makeQuery(id+"F12.opExtrude","SWEPT_FACE",FACE,{"disambiguationData":[OSD([sQuery(id+"F11.wireOp",EDGE,"E23")])]})]})]});
            var Q6;
            {var subQ0=makeQuery(id+"F9.opExtrude","SWEPT_FACE",FACE,{"disambiguationData":[OSD([sQuery(id+"F8.wireOp",EDGE,"E15")])]});var subQ1=sQuery(id+"F6.wireOp",EDGE,"E13.top");var subQ2=sQuery(id+"F6.wireOp",EDGE,"E13.right");var subQ3=sQuery(id+"F6.wireOp",EDGE,"E13.left");var subQ4=sQuery(id+"F6.wireOp",EDGE,"E13.bottom");var subQ5=makeQuery(id+"F7.opExtrude","CAP_FACE",FACE,{"disambiguationData":[OSD([subQ4,subQ1,subQ3,subQ2])],"isStart":false});var subQ6=sQuery(id+"F0.wireOp",EDGE,"E0.left");var subQ7=sQuery(id+"F0.wireOp",EDGE,"E0.bottom");Q6=makeQuery(id+"F18.opFillet","BLEND_EDGE",EDGE,{"blendedFrom":[makeQuery(id+"F17.opFillet","BLEND_EDGE",EDGE,{"blendedFrom":[makeQuery(id+"F7.boolean.opBoolean","MERGE",EDGE,{"derivedFrom":[makeQuery(id+"F1.opExtrude","SWEPT_EDGE",EDGE,{"disambiguationData":[OSD([subQ7,subQ6])]}),makeQuery(id+"F7.opExtrude","SWEPT_EDGE",EDGE,{"disambiguationData":[OSD([subQ1,subQ2])]})]}),makeQuery(id+"F13.boolean.opBoolean","MERGE",FACE,{"derivedFrom":[makeQuery(id+"F9.boolean.opBoolean","SPLIT",FACE,{"disambiguationData":[TD([makeQuery(id+"F1.opExtrude","SWEPT_FACE",FACE,{"disambiguationData":[OSD([subQ7])]})])],"derivedFrom":subQ5}),makeQuery(id+"F9.boolean.opBoolean","SPLIT",FACE,{"disambiguationData":[TD([makeQuery(id+"F9.opExtrude","SWEPT_FACE",FACE,{"disambiguationData":[OSD([sQuery(id+"F8.wireOp",EDGE,"E14")])]})])],"derivedFrom":subQ5}),makeQuery(id+"F13.opExtrude","SWEPT_FACE",FACE,{"disambiguationData":[OSD([subQ1])]})]})],"blendedInto":[makeQuery(id+"F13.boolean.opBoolean","MERGE",FACE,{"derivedFrom":[makeQuery(id+"F9.boolean.opBoolean","SPLIT",FACE,{"disambiguationData":[TD([makeQuery(id+"F1.opExtrude","SWEPT_FACE",FACE,{"disambiguationData":[OSD([subQ7])]})])],"derivedFrom":subQ5}),makeQuery(id+"F9.boolean.opBoolean","SPLIT",FACE,{"disambiguationData":[TD([makeQuery(id+"F9.opExtrude","SWEPT_FACE",FACE,{"disambiguationData":[OSD([sQuery(id+"F8.wireOp",EDGE,"E14")])]})])],"derivedFrom":subQ5}),makeQuery(id+"F13.opExtrude","SWEPT_FACE",FACE,{"disambiguationData":[OSD([subQ1])]})]})]}),makeQuery(id+"F12.boolean.opBoolean","MERGE",FACE,{"derivedFrom":[subQ0,makeQuery(id+"F12.opExtrude","SWEPT_FACE",FACE,{"disambiguationData":[OSD([sQuery(id+"F11.wireOp",EDGE,"E23")])]})]})],"blendedInto":[makeQuery(id+"F12.boolean.opBoolean","MERGE",FACE,{"derivedFrom":[subQ0,makeQuery(id+"F12.opExtrude","SWEPT_FACE",FACE,{"disambiguationData":[OSD([sQuery(id+"F11.wireOp",EDGE,"E23")])]})]})]});}
            fillet(context, id + "F19", {"entities" : qUnion([Q0, Q1, Q2, Q3, Q4, Q5, Q6]), "radius" : 5 * mm, "tangentPropagation" : true, "allowEdgeOverflow" : false});
        }
        {
            var Q0;
            Q0=makeQuery(id+"F13.boolean.opBoolean","COPY",EDGE,{"derivedFrom":makeQuery(id+"F13.opExtrude","SWEPT_EDGE",EDGE,{"disambiguationData":[OSD([sQuery(id+"F10.wireOp",EDGE,"E19"),sQuery(id+"F10.wireOp",EDGE,"E22.bottom"),sQuery(id+"F10.wireOp",EDGE,"E22.left")])]})});
            var Q1;
            Q1=makeQuery(id+"F13.boolean.opBoolean","COPY",EDGE,{"derivedFrom":makeQuery(id+"F13.opExtrude","SWEPT_EDGE",EDGE,{"disambiguationData":[OSD([sQuery(id+"F10.wireOp",EDGE,"E19"),sQuery(id+"F10.wireOp",EDGE,"E22.bottom"),sQuery(id+"F10.wireOp",EDGE,"E22.right")])]})});
            chamfer(context, id + "F20", {"entities" : qUnion([Q0, Q1]), "width" : 1.3 * mm, "tangentPropagation" : true});
        }
    });
